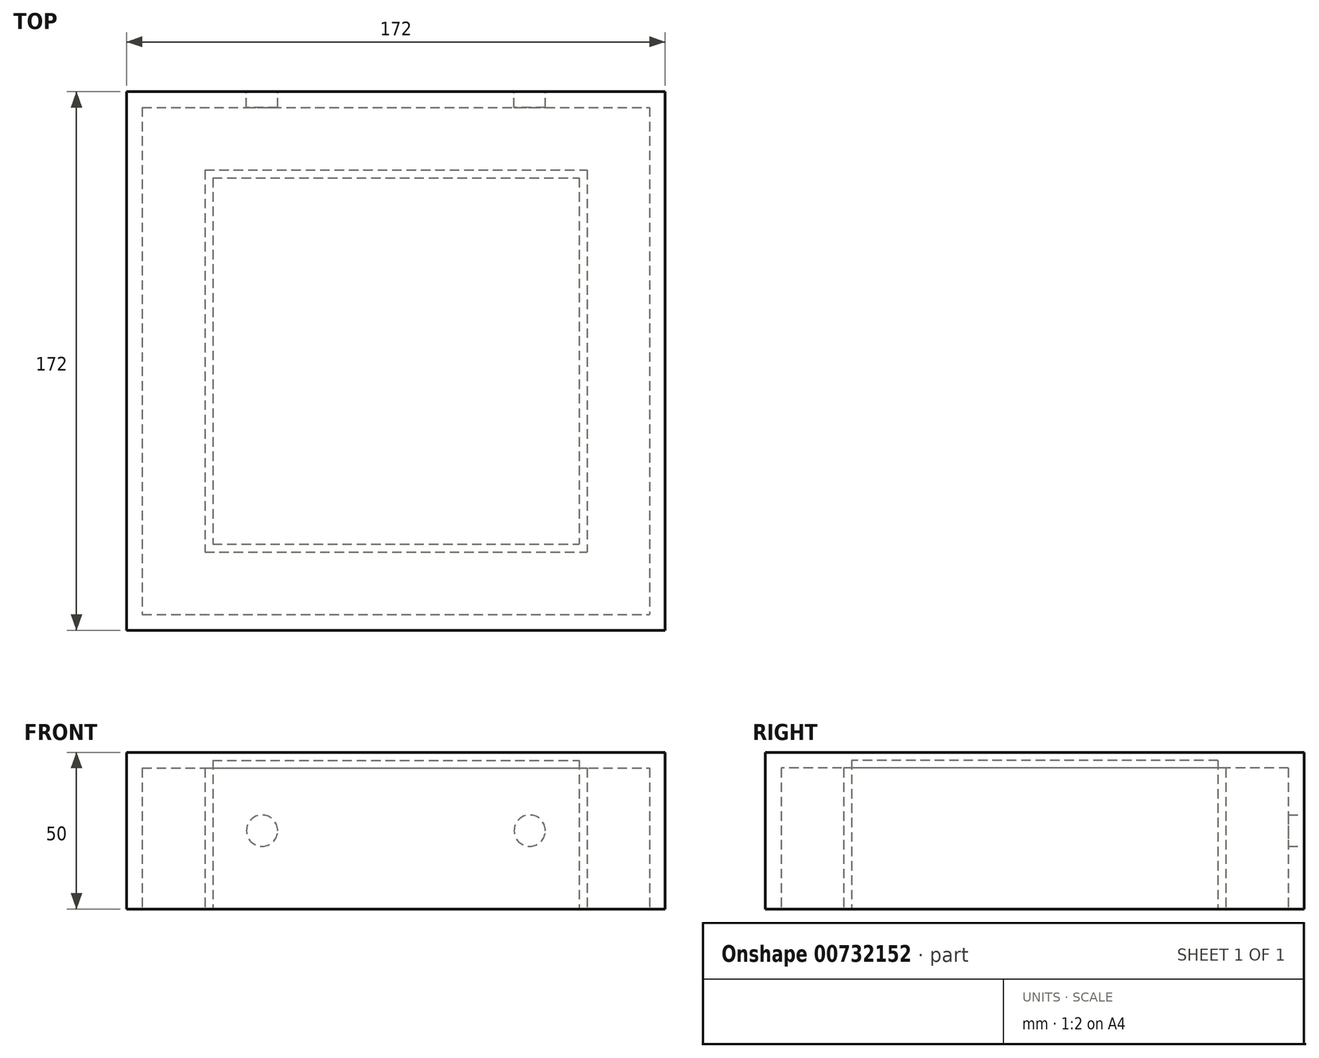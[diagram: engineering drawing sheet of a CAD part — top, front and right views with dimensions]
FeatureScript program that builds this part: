
annotation { "Feature Type Name" : "Feature", "Feature Type Description" : "" }
export const myFeature = defineFeature(function(context is Context, id is Id, definition is map)
    precondition{}
    {
        {
            var Q0;
            Q0=qCreatedBy(makeId("Top.planeOp"),FACE);
            var sketch = newSketch(context, id + "F0", { "sketchPlane" : qUnion([Q0])});
            skLineSegment(sketch, "E0.bottom", {"start": v(-86, 86) * mm, "end": v(86, 86) * mm});
            skLineSegment(sketch, "E0.top", {"start": v(-86, -86) * mm, "end": v(86, -86) * mm});
            skLineSegment(sketch, "E0.left", {"start": v(-86, 86) * mm, "end": v(-86, -86) * mm});
            skLineSegment(sketch, "E0.right", {"start": v(86, 86) * mm, "end": v(86, -86) * mm});
            skPoint(sketch, "E0.middle", {"position": v(0, 0) * mm});
            skSolve(sketch);
        }
        {
            var Q0;
            Q0=qSketchRegion(id+"F0",true);
            extrude(context, id + "F1", {"entities" : qUnion([Q0]), "depth" : 50 * mm, "offsetDistance" : 25 * mm});
        }
        {
            var Q0;
            Q0=qCreatedBy(makeId("Top.planeOp"),FACE);
            var sketch = newSketch(context, id + "F2", { "sketchPlane" : qUnion([Q0])});
            skLineSegment(sketch, "E1.bottom", {"start": v(-81, 81) * mm, "end": v(81, 81) * mm});
            skLineSegment(sketch, "E1.top", {"start": v(-81, -81) * mm, "end": v(81, -81) * mm});
            skLineSegment(sketch, "E1.left", {"start": v(-81, 81) * mm, "end": v(-81, -81) * mm});
            skLineSegment(sketch, "E1.right", {"start": v(81, 81) * mm, "end": v(81, -81) * mm});
            skPoint(sketch, "E1.middle", {"position": v(0, 0) * mm});
            skLineSegment(sketch, "E2.bottom", {"start": v(-61, 61) * mm, "end": v(61, 61) * mm});
            skLineSegment(sketch, "E2.top", {"start": v(-61, -61) * mm, "end": v(61, -61) * mm});
            skLineSegment(sketch, "E2.left", {"start": v(-61, 61) * mm, "end": v(-61, -61) * mm});
            skLineSegment(sketch, "E2.right", {"start": v(61, 61) * mm, "end": v(61, -61) * mm});
            skSolve(sketch);
        }
        {
            var Q0;
            Q0=qSketchRegion(id+"F2",true);
            extrude(context, id + "F3", {"entities" : qUnion([Q0]), "operationType" : NewBodyOperationType.REMOVE, "depth" : 45 * mm, "offsetDistance" : 25 * mm});
        }
        {
            var Q0;
            Q0=makeQuery(id+"F3.boolean.opBoolean","SPLIT",FACE,{"disambiguationData":[TD([makeQuery(id+"F3.opExtrude","SWEPT_FACE",FACE,{"disambiguationData":[OSD([sQuery(id+"F2.wireOp",EDGE,"E2.bottom")])]})])],"derivedFrom":makeQuery(id+"F1.opExtrude","CAP_FACE",FACE,{"disambiguationData":[OSD([sQuery(id+"F0.wireOp",EDGE,"E0.bottom"),sQuery(id+"F0.wireOp",EDGE,"E0.top"),sQuery(id+"F0.wireOp",EDGE,"E0.left"),sQuery(id+"F0.wireOp",EDGE,"E0.right")])],"isStart":true})});
            shell(context, id + "F4", {"entities" : qUnion([Q0]), "thickness" : 2.5 * mm});
        }
        {
            var Q0;
            Q0=makeQuery(id+"F1.opExtrude","SWEPT_FACE",FACE,{"disambiguationData":[OSD([sQuery(id+"F0.wireOp",EDGE,"E0.bottom")])]});
            var sketch = newSketch(context, id + "F5", { "sketchPlane" : qUnion([Q0])});
            skCircle(sketch, "E3", {"center": v(42.74, 25) * mm, "radius": 5 * mm});
            skCircle(sketch, "E4.MirrorC", {"center": v(-42.74, 25) * mm, "radius": 5 * mm});
            skSolve(sketch);
        }
        {
            var Q0;
            Q0=qSketchRegion(id+"F5",true);
            extrude(context, id + "F6", {"entities" : qUnion([Q0]), "operationType" : NewBodyOperationType.REMOVE, "oppositeDirection" : true, "depth" : 9.5 * mm, "offsetDistance" : 25 * mm});
        }
    });
